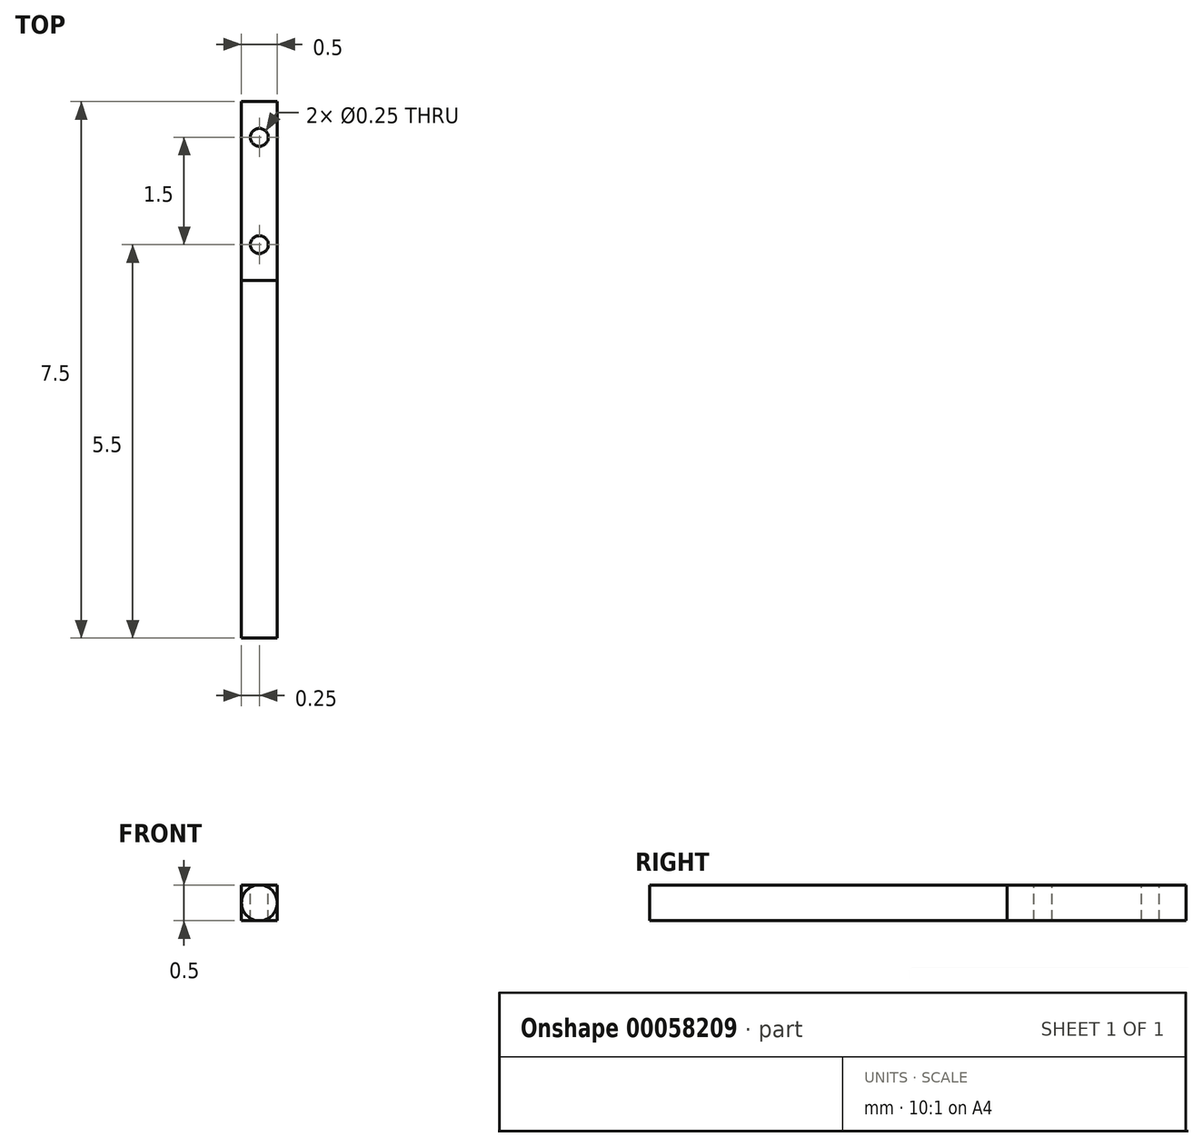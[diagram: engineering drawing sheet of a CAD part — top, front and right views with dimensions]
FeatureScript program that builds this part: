
annotation { "Feature Type Name" : "Feature", "Feature Type Description" : "" }
export const myFeature = defineFeature(function(context is Context, id is Id, definition is map)
    precondition{}
    {
        {
            var Q0;
            Q0=qCreatedBy(makeId("Front.planeOp"),FACE);
            var sketch = newSketch(context, id + "F0", { "sketchPlane" : qUnion([Q0])});
            skCircle(sketch, "E0", {"center": v(0, 0) * mm, "radius": 0.25 * mm});
            skSolve(sketch);
        }
        {
            var Q0;
            Q0=qSketchRegion(id+"F0",true);
            extrude(context, id + "F1", {"entities" : qUnion([Q0]), "endBound" : BoundingType.SYMMETRIC, "depth" : 7.5 * mm});
        }
        {
            var Q0;
            Q0=makeQuery(id+"F1.opExtrude","CAP_FACE",FACE,{"disambiguationData":[OSD([sQuery(id+"F0.wireOp",EDGE,"E0")])],"isStart":true});
            var sketch = newSketch(context, id + "F2", { "sketchPlane" : qUnion([Q0])});
            skLineSegment(sketch, "E1.rect.bottom", {"start": v(0.25, 0.25) * mm, "end": v(-0.25, 0.25) * mm});
            skLineSegment(sketch, "E1.rect.top", {"start": v(0.25, -0.25) * mm, "end": v(-0.25, -0.25) * mm});
            skLineSegment(sketch, "E1.rect.left", {"start": v(0.25, 0.25) * mm, "end": v(0.25, -0.25) * mm});
            skLineSegment(sketch, "E1.rect.right", {"start": v(-0.25, 0.25) * mm, "end": v(-0.25, -0.25) * mm});
            skPoint(sketch, "E1.rect.middle", {"position": v(0, 0) * mm});
            skSolve(sketch);
        }
        {
            var Q0;
            Q0=qSketchRegion(id+"F2",true);
            extrude(context, id + "F3", {"entities" : qUnion([Q0]), "operationType" : NewBodyOperationType.ADD, "oppositeDirection" : true, "depth" : 2.5 * mm});
        }
        {
            var Q0;
            Q0=makeQuery(id+"F3.opExtrude","SWEPT_FACE",FACE,{"disambiguationData":[OSD([sQuery(id+"F2.wireOp",EDGE,"E1.rect.bottom")])]});
            var sketch = newSketch(context, id + "F4", { "sketchPlane" : qUnion([Q0])});
            skCircle(sketch, "E2", {"center": v(0, 3.25) * mm, "radius": 0.12 * mm});
            skPoint(sketch, "E2.centerSnap0", {"position": v(0, 3.75) * mm});
            skCircle(sketch, "E3", {"center": v(0, 1.75) * mm, "radius": 0.12 * mm});
            skSolve(sketch);
        }
        {
            var Q0;
            Q0=qSketchRegion(id+"F4",true);
            extrude(context, id + "F5", {"entities" : qUnion([Q0]), "operationType" : NewBodyOperationType.REMOVE, "oppositeDirection" : true, "depth" : 25 * mm});
        }
    });
